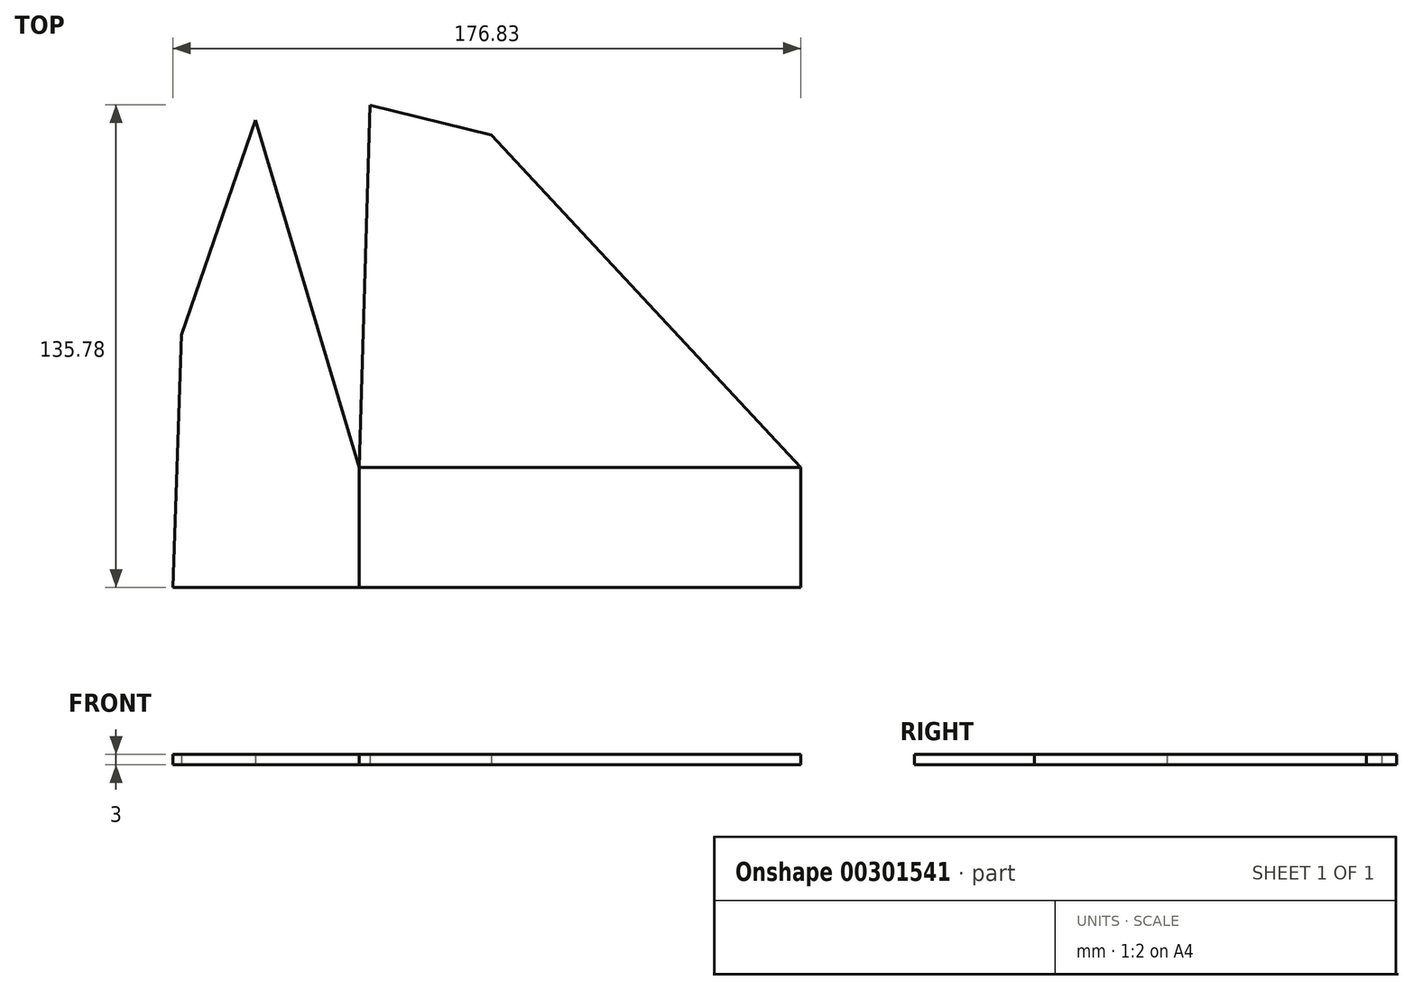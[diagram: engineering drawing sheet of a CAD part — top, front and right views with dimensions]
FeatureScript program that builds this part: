
annotation { "Feature Type Name" : "Feature", "Feature Type Description" : "" }
export const myFeature = defineFeature(function(context is Context, id is Id, definition is map)
    precondition{}
    {
        {
            var Q0;
            Q0=qCreatedBy(makeId("Top.planeOp"),FACE);
            var sketch = newSketch(context, id + "F0", { "sketchPlane" : qUnion([Q0])});
            skLineSegment(sketch, "E0.bottom", {"start": v(0, 0) * mm, "end": v(124.34, 0) * mm});
            skLineSegment(sketch, "E0.top", {"start": v(0, 33.72) * mm, "end": v(124.34, 33.72) * mm});
            skLineSegment(sketch, "E0.left", {"start": v(0, 0) * mm, "end": v(0, 33.72) * mm});
            skLineSegment(sketch, "E0.right", {"start": v(124.34, 0) * mm, "end": v(124.34, 33.72) * mm});
            skLineSegment(sketch, "E1", {"start": v(0, 33.72) * mm, "end": v(3.1, 135.78) * mm});
            skLineSegment(sketch, "E2", {"start": v(3.1, 135.78) * mm, "end": v(37.18, 127.27) * mm});
            skLineSegment(sketch, "E3", {"start": v(37.18, 127.27) * mm, "end": v(124.34, 33.72) * mm});
            skLineSegment(sketch, "E4", {"start": v(0, 33.72) * mm, "end": v(-29.18, 131.56) * mm});
            skLineSegment(sketch, "E5", {"start": v(-29.18, 131.56) * mm, "end": v(-50.04, 71.09) * mm});
            skLineSegment(sketch, "E6", {"start": v(-50.04, 71.09) * mm, "end": v(-52.5, 0) * mm});
            skLineSegment(sketch, "E7", {"start": v(0, 0) * mm, "end": v(-52.5, 0) * mm});
            skLineSegment(sketch, "E8", {"start": v(-52.5, 0) * mm, "end": v(-119.44, 9.34) * mm});
            skLineSegment(sketch, "E9", {"start": v(-119.44, 9.34) * mm, "end": v(-50.04, 71.09) * mm});
            skLineSegment(sketch, "E10", {"start": v(-50.04, 71.09) * mm, "end": v(-153.1, 67.42) * mm});
            skLineSegment(sketch, "E11", {"start": v(-153.1, 67.42) * mm, "end": v(-119.44, 9.34) * mm});
            skLineSegment(sketch, "E12", {"start": v(-153.1, 67.42) * mm, "end": v(-58.02, 152.92) * mm});
            skLineSegment(sketch, "E13", {"start": v(-58.02, 152.92) * mm, "end": v(-50.04, 71.09) * mm});
            skArc(sketch, "E14", {"start": v(3.1, 135.78) * mm, "mid": v(-13.21, 134.97) * mm, "end": v(-29.18, 131.56) * mm, "construction": true});
            skSolve(sketch);
        }
        {
            var Q0;
            Q0=makeQuery(id+"F0.imprint","IMPRINT",FACE,{"disambiguationData":[TD([[makeQuery(id+"F0.imprint","IMPRINT",EDGE,{"derivedFrom":sQuery(id+"F0.wireOp",EDGE,"E0.left")}),1.0]])]});
            var Q1;
            Q1=makeQuery(id+"F0.imprint","IMPRINT",FACE,{"disambiguationData":[TD([[makeQuery(id+"F0.imprint","IMPRINT",EDGE,{"derivedFrom":sQuery(id+"F0.wireOp",EDGE,"E0.top")}),1.0]])]});
            extrude(context, id + "F1", {"entities" : qUnion([Q0, Q1]), "depth" : 3 * mm});
        }
        {
            var Q0;
            Q0=makeQuery(id+"F0.imprint","IMPRINT",FACE,{"disambiguationData":[TD([[makeQuery(id+"F0.imprint","IMPRINT",EDGE,{"derivedFrom":sQuery(id+"F0.wireOp",EDGE,"E0.bottom")}),1.0]])]});
            extrude(context, id + "F2", {"entities" : qUnion([Q0]), "depth" : 3 * mm});
        }
    });
